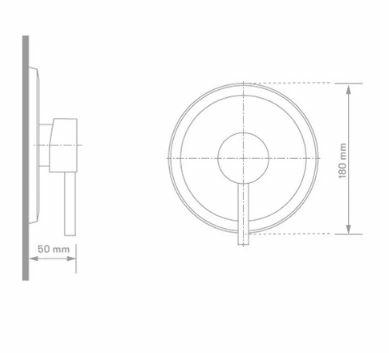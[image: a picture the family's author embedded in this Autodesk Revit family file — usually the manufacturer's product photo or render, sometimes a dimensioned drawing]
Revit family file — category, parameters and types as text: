
# Revit family: 01-2455-11 PORTARROLLO METALICO QUADRA
name_source: partatom
category: Plumbing Fixtures
revit_build: Autodesk Revit 2018 (Build: 20170223_1515(x64)
units: mm (PartAtom-declared; Revit-internal decimal feet)

## family parameters
Cut with Voids When Loaded = No
Host = Face
OmniClass Number = 23.31.11.00
Part Type = Normal
Room Calculation Point = No
Round Connector Dimension = Use Diameter
Shared = No

## types (1)
- 01-2455-11
    Alto portarrollo = 94 mm  [stored 0.308399 ft]
    Ancho Soporte = 22 mm  [stored 0.0721785 ft]
    Ancho portarrollo = 170 mm  [stored 0.557743 ft]
    CW Connection = Yes
    Default Elevation = 0 mm  [stored 0 ft]
    Description = PORTARROLLO
    HW Connection = Yes
    Link Ficha Tecnica = http://infotecnica.gricol.com
    Manufacturer = Gricol
    Model = 01-2455-11
    Product Name = PORTARROLLO METALICO QUADRA
    Profundidad = 75 mm  [stored 0.246063 ft]
    Soporte y portarrollo = Metal Laton Cromado
    Type Image = PORTARROLLO METALICO QUADRA.JPG
    URL = https://www.gricol.com
    Vent Connection = No
    Waste Connection = No

note: [stored X ft] marks values corroborated as IEEE doubles in the binary element streams (Revit-internal decimal feet)

## geometry (parser evidence)
native form markers: Blend x2, Sweep x4
no freeform markers — native parametric forms only
